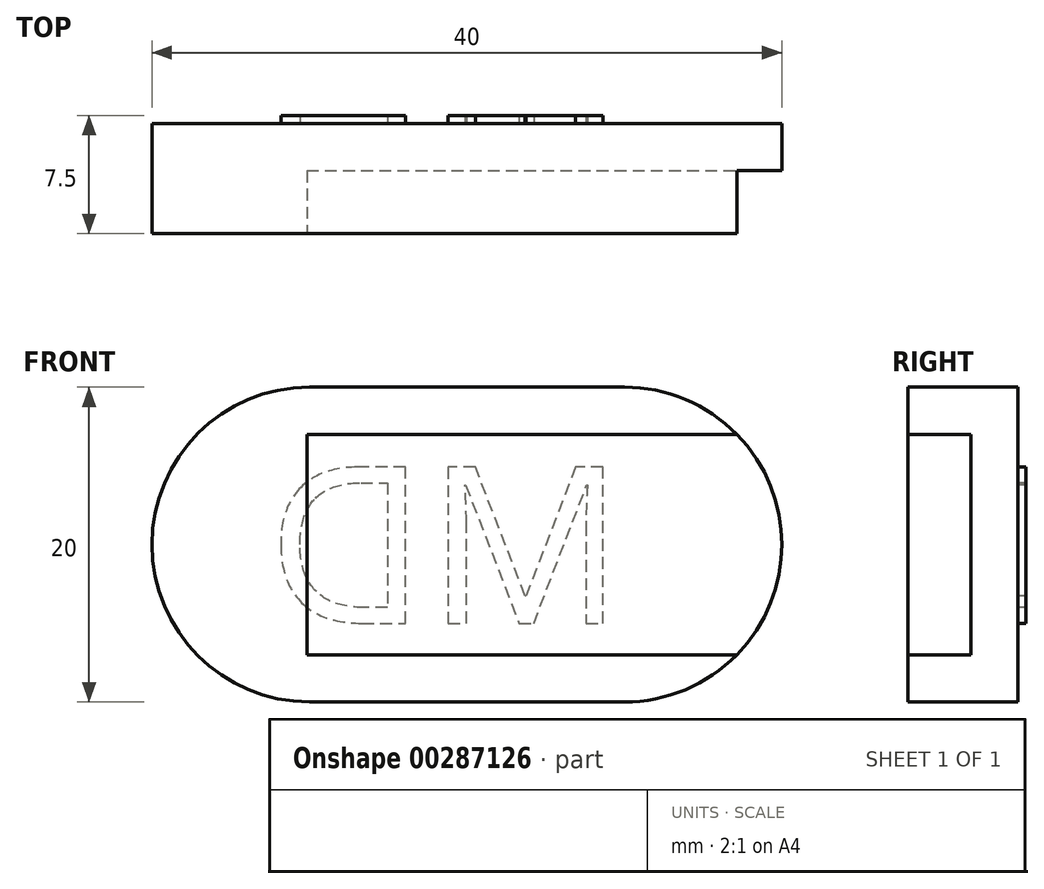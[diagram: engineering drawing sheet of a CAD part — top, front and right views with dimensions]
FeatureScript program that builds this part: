
annotation { "Feature Type Name" : "Feature", "Feature Type Description" : "" }
export const myFeature = defineFeature(function(context is Context, id is Id, definition is map)
    precondition{}
    {
        {
            var Q0;
            Q0=qCreatedBy(makeId("Front.planeOp"),FACE);
            var sketch = newSketch(context, id + "F0", { "sketchPlane" : qUnion([Q0])});
            skCircle(sketch, "E0", {"center": v(-29.84, 0) * mm, "radius": 10 * mm});
            skCircle(sketch, "E1", {"center": v(-9.84, 0) * mm, "radius": 10 * mm});
            skLineSegment(sketch, "E2", {"start": v(-29.84, -10) * mm, "end": v(-9.84, -10) * mm});
            skLineSegment(sketch, "E3", {"start": v(-29.84, 10) * mm, "end": v(-9.84, 10) * mm});
            skSolve(sketch);
        }
        {
            var Q0;
            {var subQ0=sQuery(id+"F0.wireOp",EDGE,"E0");var subQ1=makeQuery(id+"F0.imprint","INTERSECT",VERTEX,{"derivedFrom":[subQ0,sQuery(id+"F0.wireOp",EDGE,"E3")]});Q0=makeQuery(id+"F0.imprint","IMPRINT",FACE,{"disambiguationData":[TD([[makeQuery(id+"F0.imprint","IMPRINT",EDGE,{"disambiguationData":[TD([[subQ1,1.0]])],"derivedFrom":subQ0}),1.0]])]});}
            var Q1;
            {var subQ0=sQuery(id+"F0.wireOp",EDGE,"E3");Q1=makeQuery(id+"F0.imprint","IMPRINT",FACE,{"disambiguationData":[TD([[makeQuery(id+"F0.imprint","IMPRINT",EDGE,{"derivedFrom":subQ0}),-1.0]])]});}
            var Q2;
            {var subQ0=sQuery(id+"F0.wireOp",EDGE,"E1");var subQ1=makeQuery(id+"F0.imprint","INTERSECT",VERTEX,{"derivedFrom":[subQ0,sQuery(id+"F0.wireOp",EDGE,"E3")]});Q2=makeQuery(id+"F0.imprint","IMPRINT",FACE,{"disambiguationData":[TD([[makeQuery(id+"F0.imprint","IMPRINT",EDGE,{"disambiguationData":[TD([[subQ1,-1.0]])],"derivedFrom":subQ0}),1.0]])]});}
            var Q3;
            {var subQ0=sQuery(id+"F0.wireOp",EDGE,"E2");Q3=makeQuery(id+"F0.imprint","IMPRINT",FACE,{"disambiguationData":[TD([[makeQuery(id+"F0.imprint","IMPRINT",EDGE,{"derivedFrom":subQ0}),1.0]])]});}
            extrude(context, id + "F1", {"entities" : qUnion([Q0, Q1, Q2, Q3]), "depth" : 7 * mm});
        }
        {
            var Q0;
            Q0=makeQuery(id+"F1.opExtrude","CAP_FACE",FACE,{"disambiguationData":[OSD([sQuery(id+"F0.wireOp",EDGE,"E0"),sQuery(id+"F0.wireOp",EDGE,"E1"),sQuery(id+"F0.wireOp",EDGE,"E2"),sQuery(id+"F0.wireOp",EDGE,"E3")])],"isStart":false});
            var sketch = newSketch(context, id + "F2", { "sketchPlane" : qUnion([Q0])});
            skLineSegment(sketch, "E4.bottom", {"start": v(-30, 7) * mm, "end": v(30, 7) * mm});
            skLineSegment(sketch, "E4.top", {"start": v(-30, -7) * mm, "end": v(30, -7) * mm});
            skLineSegment(sketch, "E4.left", {"start": v(-30, 7) * mm, "end": v(-30, -7) * mm});
            skLineSegment(sketch, "E4.right", {"start": v(30, 7) * mm, "end": v(30, -7) * mm});
            skPoint(sketch, "E4.middle", {"position": v(0, 0) * mm});
            skPoint(sketch, "E5", {"position": v(-2.7, 7) * mm});
            skPoint(sketch, "E6", {"position": v(-2.7, -7) * mm});
            skSolve(sketch);
        }
        {
            var Q0;
            {var subQ0=sQuery(id+"F2.wireOp",EDGE,"E4.right");Q0=makeQuery(id+"F2.imprint","IMPRINT",FACE,{"disambiguationData":[TD([[makeQuery(id+"F2.imprint","IMPRINT",EDGE,{"derivedFrom":subQ0}),-1.0]])]});}
            var Q1;
            {var subQ0=sQuery(id+"F2.wireOp",EDGE,"E4.left");Q1=makeQuery(id+"F2.imprint","IMPRINT",FACE,{"disambiguationData":[TD([[makeQuery(id+"F2.imprint","IMPRINT",EDGE,{"derivedFrom":subQ0}),1.0]])]});}
            extrude(context, id + "F3", {"entities" : qUnion([Q0, Q1]), "operationType" : NewBodyOperationType.REMOVE, "oppositeDirection" : true, "depth" : 4 * mm});
        }
        {
            var Q0;
            Q0=makeQuery(id+"F1.opExtrude","CAP_FACE",FACE,{"disambiguationData":[OSD([sQuery(id+"F0.wireOp",EDGE,"E0"),sQuery(id+"F0.wireOp",EDGE,"E1"),sQuery(id+"F0.wireOp",EDGE,"E2"),sQuery(id+"F0.wireOp",EDGE,"E3")])],"isStart":true});
            var sketch = newSketch(context, id + "F4", { "sketchPlane" : qUnion([Q0])});
            skText(sketch, "E7", { "text": "MD", "fontName": "OpenSans-Regular.ttf"});
            const initialGuessF4  = {"E7": [0.00984, -0.005, 1, 0, 0.01]};
            skSetInitialGuess(sketch, initialGuessF4);
            skSolve(sketch);
        }
        {
            var Q0;
            Q0 = qSketchRegion(id + "F4", true);
            extrude(context, id + "F5", {"entities" : qUnion([Q0]), "operationType" : NewBodyOperationType.ADD, "depth" : .5 * mm});
        }
    });
